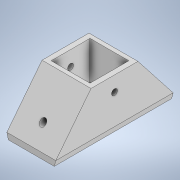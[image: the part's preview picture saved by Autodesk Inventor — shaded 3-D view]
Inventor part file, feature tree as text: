
AUTODESK INVENTOR PART (.ipt)
format: ipt  version: 2022 (Build 260153000, 153)  size: 186,880 bytes
history: native  units: mm
features: extrude x9, sketch x9, plane x1
ambient origin geometry x8: Origin, YZ Plane, XZ Plane, XY Plane, X Axis, Y Axis, Z Axis, Center Point
bodies: Solid1 (feature_tree)
feature tree (19):
  extrude  "Extrusion1"  Depth=40.0mm TaperAngle=360.0deg
  extrude  "Extrusion2"  Depth=13.25mm
  extrude  "Extrusion4"  Depth=2.0mm TaperAngle=0.0deg
  extrude  "Extrusion5"  Depth=12.7mm
  extrude  "Extrusion6"  Depth=3.0mm
  extrude  "Extrusion7"  Depth=30.0mm TaperAngle=0.0deg
  plane  "Work Plane1"
  extrude  "Extrusion8"  Depth=26.0mm
  extrude  "Extrusion9"  Depth=25.4mm TaperAngle=0.0deg
  extrude  "Extrusion10"  TaperAngle=0.0deg  [1 undecoded]
  sketch  "Sketch1"  dims[d2=4.0mm d3=40.0mm d5=360.0deg]
  sketch  "Sketch2"  dims[d16=5.0mm d17=0.0mm d18=13.25mm]
  sketch  "Sketch4"  dims[d19=2.0mm d20=0.0mm d26=73.5mm d27=0.0mm]
  sketch  "Sketch5"  dims[d28=30.0mm d29=0.0mm d30=12.7mm]
  sketch  "Sketch6"  dims[d31=12.7mm d32=3.0mm]
  sketch  "Sketch7"  dims[d33=3.0mm d34=30.0mm d35=0.0mm]
  sketch  "Sketch8"  dims[d37=13.0mm d38=26.0mm]
  sketch  "Sketch9"  dims[d39=26.0mm d40=25.4mm d41=0.0mm]
  sketch  "Sketch10"  dims[d43=4.0mm d44=0.0mm d45=0.0mm d47=4.0mm d48=10.0mm d49=0.0mm d50=10.0mm d51=25.0mm d52=0.0mm d53=0.0mm]
note: 1 required parameter value undecoded (feature->parameter linkage not recoverable at this tier; creation-order binding heuristic only, values carry confidence <= 0.55)
